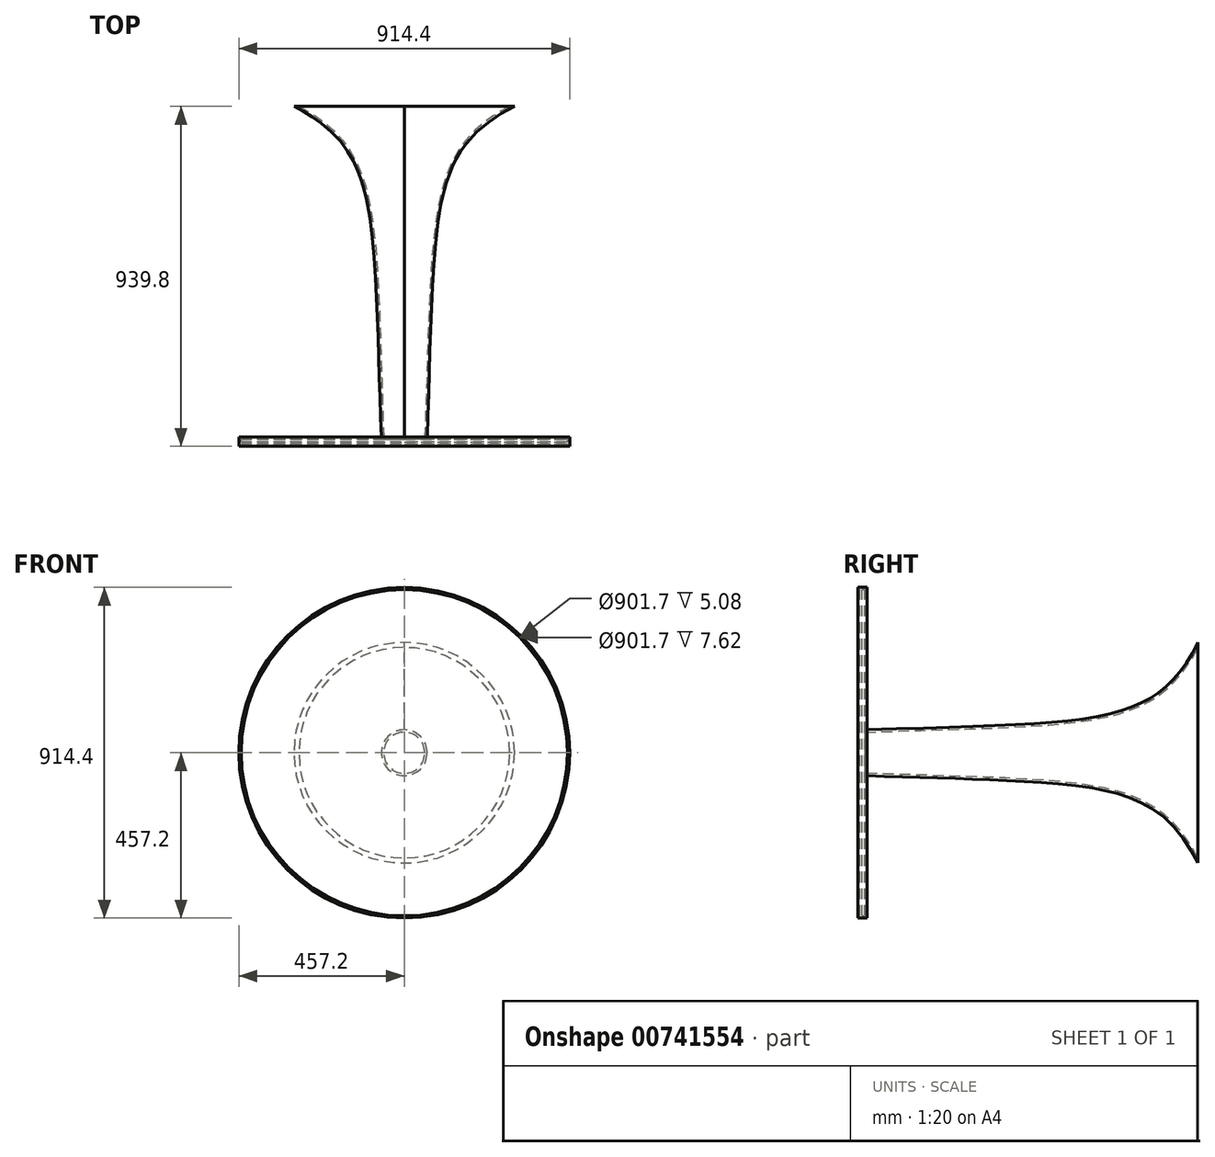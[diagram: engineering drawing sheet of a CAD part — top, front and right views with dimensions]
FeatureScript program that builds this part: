
annotation { "Feature Type Name" : "Feature", "Feature Type Description" : "" }
export const myFeature = defineFeature(function(context is Context, id is Id, definition is map)
    precondition{}
    {
        {
            var Q0;
            Q0=qCreatedBy(makeId("Front.planeOp"),FACE);
            var sketch = newSketch(context, id + "F0", { "sketchPlane" : qUnion([Q0])});
            skLineSegment(sketch, "E0", {"start": v(-757.24, 0) * mm, "end": v(751.6, 0) * mm, "construction": true});
            skLineSegment(sketch, "E1", {"start": v(0, 471.27) * mm, "end": v(0, -392.26) * mm, "construction": true});
            skCircle(sketch, "E2", {"center": v(0, 0) * mm, "radius": 457.2 * mm});
            skSolve(sketch);
        }
        {
            var Q0;
            Q0=makeQuery(id+"F0.imprint","IMPRINT",FACE,{"disambiguationData":[TD([[makeQuery(id+"F0.imprint","IMPRINT",EDGE,{"derivedFrom":sQuery(id+"F0.wireOp",EDGE,"E2")}),1.0]])]});
            extrude(context, id + "F1", {"entities" : qUnion([Q0]), "depth" : 25.4 * mm, "offsetDistance" : 25.4 * mm});
        }
        {
            var Q0;
            Q0=makeQuery(id+"F1.opExtrude","CAP_FACE",FACE,{"disambiguationData":[OSD([sQuery(id+"F0.wireOp",EDGE,"E2")])],"isStart":false});
            var sketch = newSketch(context, id + "F2", { "sketchPlane" : qUnion([Q0])});
            skCircle(sketch, "E3.0", {"center": v(0, 0) * mm, "radius": 450.85 * mm});
            skSolve(sketch);
        }
        {
            var Q0;
            Q0=makeQuery(id+"F2.imprint","IMPRINT",FACE,{"disambiguationData":[TD([[makeQuery(id+"F2.imprint","IMPRINT",EDGE,{"derivedFrom":sQuery(id+"F2.wireOp",EDGE,"E3.0")}),1.0]])]});
            extrude(context, id + "F3", {"entities" : qUnion([Q0]), "operationType" : NewBodyOperationType.REMOVE, "oppositeDirection" : true, "depth" : 5.08 * mm, "offsetDistance" : 25.4 * mm});
        }
        {
            var Q0;
            Q0=qCreatedBy(makeId("Right.planeOp"),FACE);
            var sketch = newSketch(context, id + "F4", { "sketchPlane" : qUnion([Q0])});
            skFitSpline(sketch, "E4", {"points": [v(0, 63.5) * mm, v(914.4, 304.8) * mm], "startDerivative": vector(1919.53, 64.41) * mm, "endDerivative": vector(363.33, 710.78) * mm});
            skLineSegment(sketch, "E5", {"start": v(0, 0) * mm, "end": v(1126.24, 0) * mm, "construction": true});
            skLineSegment(sketch, "E6", {"start": v(914.4, 304.8) * mm, "end": v(914.4, 0) * mm});
            skLineSegment(sketch, "E7", {"start": v(914.4, 0) * mm, "end": v(0, 0) * mm});
            skLineSegment(sketch, "E8", {"start": v(0, 63.5) * mm, "end": v(0, 0) * mm});
            skSolve(sketch);
        }
        {
            var Q0;
            Q0=makeQuery(id+"F4.imprint","IMPRINT",FACE,{"disambiguationData":[TD([[makeQuery(id+"F4.imprint","IMPRINT",EDGE,{"derivedFrom":sQuery(id+"F4.wireOp",EDGE,"E4")}),-1.0]])]});
            var Q1;
            Q1=sQuery(id+"F4.wireOp",EDGE,"E7");
            revolve(context, id + "F5", {"operationType" : NewBodyOperationType.ADD, "surfaceOperationType" : NewSurfaceOperationType.NEW, "entities" : qUnion([Q0]), "axis" : qUnion([Q1]), "revolveType" : RevolveType.FULL});
        }
        {
            var Q0;
            Q0=makeQuery(id+"F5.opRevolve","SWEPT_FACE",FACE,{"disambiguationData":[OSD([sQuery(id+"F4.wireOp",EDGE,"E6")])]});
            shell(context, id + "F6", {"entities" : qUnion([Q0]), "thickness" : 6.35 * mm});
        }
    });
